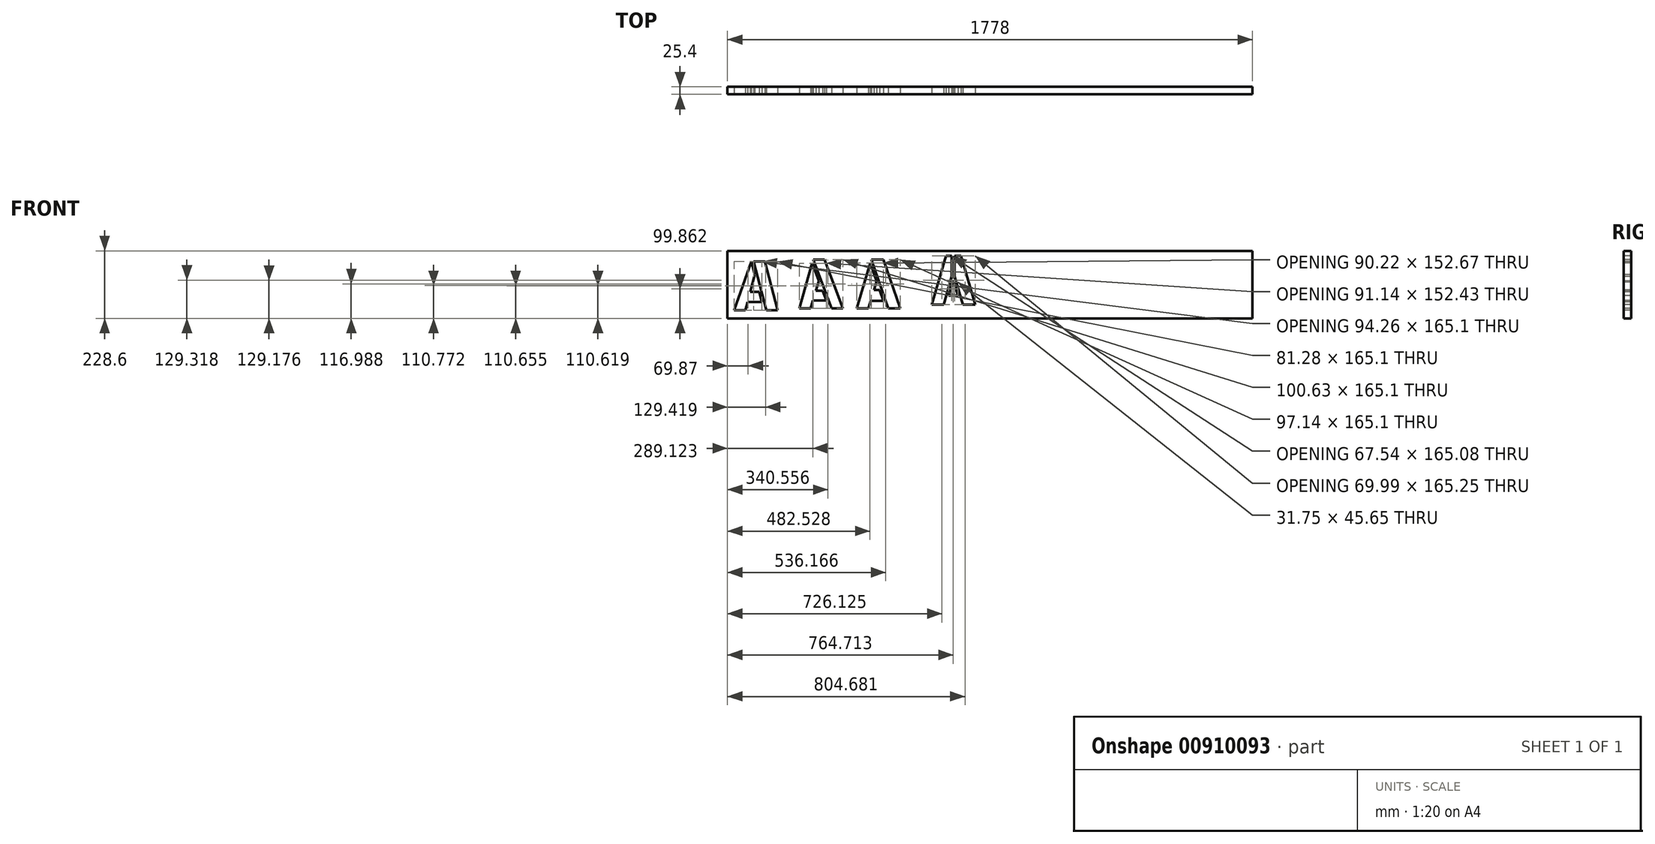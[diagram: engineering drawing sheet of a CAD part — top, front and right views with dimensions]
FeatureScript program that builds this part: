
annotation { "Feature Type Name" : "Feature", "Feature Type Description" : "" }
export const myFeature = defineFeature(function(context is Context, id is Id, definition is map)
    precondition{}
    {
        {
            var Q0;
            Q0=qCreatedBy(makeId("Front.planeOp"),FACE);
            var sketch = newSketch(context, id + "F0", { "sketchPlane" : qUnion([Q0])});
            skLineSegment(sketch, "E0.bottom", {"start": v(-868.11, -370.2) * mm, "end": v(909.89, -370.2) * mm});
            skLineSegment(sketch, "E0.top", {"start": v(-868.11, -598.8) * mm, "end": v(909.89, -598.8) * mm});
            skLineSegment(sketch, "E0.left", {"start": v(-868.11, -370.2) * mm, "end": v(-868.11, -598.8) * mm});
            skLineSegment(sketch, "E0.right", {"start": v(909.89, -370.2) * mm, "end": v(909.89, -598.8) * mm});
            skSolve(sketch);
        }
        {
            var Q0;
            Q0=makeQuery(id+"F0.imprint","IMPRINT",FACE,{"disambiguationData":[TD([[makeQuery(id+"F0.imprint","IMPRINT",EDGE,{"derivedFrom":sQuery(id+"F0.wireOp",EDGE,"E0.bottom")}),-1.0]])]});
            extrude(context, id + "F1", {"entities" : qUnion([Q0]), "depth" : 25.4 * mm, "offsetDistance" : 25.4 * mm});
        }
        {
            var Q0;
            Q0=makeQuery(id+"F1.opExtrude","CAP_FACE",FACE,{"disambiguationData":[OSD([sQuery(id+"F0.wireOp",EDGE,"E0.bottom"),sQuery(id+"F0.wireOp",EDGE,"E0.top"),sQuery(id+"F0.wireOp",EDGE,"E0.left"),sQuery(id+"F0.wireOp",EDGE,"E0.right")])],"isStart":false});
            var sketch = newSketch(context, id + "F2", { "sketchPlane" : qUnion([Q0])});
            skLineSegment(sketch, "E1", {"start": v(-845.37, -570.74) * mm, "end": v(-807.27, -570.74) * mm});
            skLineSegment(sketch, "E2", {"start": v(-807.27, -570.74) * mm, "end": v(-800.17, -543.64) * mm});
            skLineSegment(sketch, "E3", {"start": v(-790.36, -508.6) * mm, "end": v(-775.3, -451.16) * mm});
            skLineSegment(sketch, "E4", {"start": v(-736.15, -570.74) * mm, "end": v(-779.33, -405.64) * mm});
            skLineSegment(sketch, "E5", {"start": v(-779.33, -405.64) * mm, "end": v(-741.23, -405.64) * mm});
            skLineSegment(sketch, "E6", {"start": v(-741.23, -405.64) * mm, "end": v(-698.05, -570.74) * mm});
            skLineSegment(sketch, "E7.trimOffspring", {"start": v(-787.2, -405.64) * mm, "end": v(-845.37, -570.74) * mm});
            skLineSegment(sketch, "E8.trimOffspring", {"start": v(-775.3, -451.16) * mm, "end": v(-787.2, -405.64) * mm});
            skLineSegment(sketch, "E9", {"start": v(-736.15, -570.74) * mm, "end": v(-698.05, -570.74) * mm});
            skLineSegment(sketch, "E10", {"start": v(-800.17, -543.64) * mm, "end": v(-751.1, -543.66) * mm});
            skLineSegment(sketch, "E11", {"start": v(-751.1, -543.66) * mm, "end": v(-760.28, -508.61) * mm});
            skLineSegment(sketch, "E12", {"start": v(-760.28, -508.61) * mm, "end": v(-790.36, -508.6) * mm});
            skSolve(sketch);
        }
        {
            var Q0;
            Q0=makeQuery(id+"F2.imprint","IMPRINT",FACE,{"disambiguationData":[TD([[makeQuery(id+"F2.imprint","IMPRINT",EDGE,{"derivedFrom":sQuery(id+"F2.wireOp",EDGE,"E1")}),1.0]])]});
            var Q1;
            Q1=makeQuery(id+"F2.imprint","IMPRINT",FACE,{"disambiguationData":[TD([[makeQuery(id+"F2.imprint","IMPRINT",EDGE,{"derivedFrom":sQuery(id+"F2.wireOp",EDGE,"E4")}),-1.0]])]});
            extrude(context, id + "F3", {"entities" : qUnion([Q0, Q1]), "operationType" : NewBodyOperationType.REMOVE, "oppositeDirection" : true, "depth" : 25.4 * mm, "offsetDistance" : 25.4 * mm});
        }
        {
            var Q0;
            Q0=makeQuery(id+"F1.opExtrude","CAP_FACE",FACE,{"disambiguationData":[OSD([sQuery(id+"F0.wireOp",EDGE,"E0.bottom"),sQuery(id+"F0.wireOp",EDGE,"E0.top"),sQuery(id+"F0.wireOp",EDGE,"E0.left"),sQuery(id+"F0.wireOp",EDGE,"E0.right")])],"isStart":false});
            var sketch = newSketch(context, id + "F4", { "sketchPlane" : qUnion([Q0])});
            skLineSegment(sketch, "E13", {"start": v(-624.56, -564.37) * mm, "end": v(-586.46, -564.37) * mm});
            skLineSegment(sketch, "E14", {"start": v(-586.46, -564.37) * mm, "end": v(-579, -538.16) * mm});
            skLineSegment(sketch, "E15", {"start": v(-568.16, -505.31) * mm, "end": v(-558.6, -471.68) * mm});
            skLineSegment(sketch, "E16", {"start": v(-515.34, -564.37) * mm, "end": v(-577.87, -399.27) * mm});
            skLineSegment(sketch, "E17", {"start": v(-577.87, -399.27) * mm, "end": v(-539.77, -399.27) * mm});
            skLineSegment(sketch, "E18", {"start": v(-539.77, -399.27) * mm, "end": v(-477.24, -564.37) * mm});
            skLineSegment(sketch, "E19.trimOffspring", {"start": v(-581.22, -411.94) * mm, "end": v(-624.56, -564.37) * mm});
            skLineSegment(sketch, "E20", {"start": v(-515.34, -564.37) * mm, "end": v(-477.24, -564.37) * mm});
            skLineSegment(sketch, "E21", {"start": v(-579, -538.16) * mm, "end": v(-533.41, -538.16) * mm});
            skLineSegment(sketch, "E22", {"start": v(-533.41, -538.16) * mm, "end": v(-545.86, -505.31) * mm});
            skLineSegment(sketch, "E23", {"start": v(-545.86, -505.31) * mm, "end": v(-568.16, -505.31) * mm});
            skLineSegment(sketch, "E24", {"start": v(-581.22, -411.94) * mm, "end": v(-558.6, -471.68) * mm});
            skSolve(sketch);
        }
        {
            var Q0;
            Q0=makeQuery(id+"F4.imprint","IMPRINT",FACE,{"disambiguationData":[TD([[makeQuery(id+"F4.imprint","IMPRINT",EDGE,{"derivedFrom":sQuery(id+"F4.wireOp",EDGE,"E16")}),-1.0]])]});
            var Q1;
            Q1=makeQuery(id+"F4.imprint","IMPRINT",FACE,{"disambiguationData":[TD([[makeQuery(id+"F4.imprint","IMPRINT",EDGE,{"derivedFrom":sQuery(id+"F4.wireOp",EDGE,"E13")}),1.0]])]});
            extrude(context, id + "F5", {"entities" : qUnion([Q0, Q1]), "operationType" : NewBodyOperationType.REMOVE, "oppositeDirection" : true, "depth" : 25.4 * mm, "offsetDistance" : 25.4 * mm});
        }
        {
            var Q0;
            Q0=makeQuery(id+"F1.opExtrude","CAP_FACE",FACE,{"disambiguationData":[OSD([sQuery(id+"F0.wireOp",EDGE,"E0.bottom"),sQuery(id+"F0.wireOp",EDGE,"E0.top"),sQuery(id+"F0.wireOp",EDGE,"E0.left"),sQuery(id+"F0.wireOp",EDGE,"E0.right")])],"isStart":false});
            var sketch = newSketch(context, id + "F6", { "sketchPlane" : qUnion([Q0])});
            skLineSegment(sketch, "E25", {"start": v(-430.7, -564.37) * mm, "end": v(-390.87, -564.37) * mm});
            skLineSegment(sketch, "E26", {"start": v(-390.87, -564.37) * mm, "end": v(-363.14, -473.13) * mm});
            skLineSegment(sketch, "E27", {"start": v(-363.14, -473.13) * mm, "end": v(-384.3, -411.7) * mm});
            skLineSegment(sketch, "E28", {"start": v(-380.52, -399.27) * mm, "end": v(-340.22, -399.27) * mm});
            skLineSegment(sketch, "E29", {"start": v(-340.22, -399.27) * mm, "end": v(-283.37, -564.37) * mm});
            skLineSegment(sketch, "E30", {"start": v(-283.37, -564.37) * mm, "end": v(-323.67, -564.37) * mm});
            skLineSegment(sketch, "E31", {"start": v(-323.67, -564.37) * mm, "end": v(-380.52, -399.27) * mm});
            skLineSegment(sketch, "E32", {"start": v(-383.15, -538.97) * mm, "end": v(-340.47, -538.97) * mm});
            skLineSegment(sketch, "E33", {"start": v(-340.47, -538.97) * mm, "end": v(-352.88, -502.95) * mm});
            skLineSegment(sketch, "E34", {"start": v(-352.88, -502.95) * mm, "end": v(-372.2, -502.95) * mm});
            skLineSegment(sketch, "E35", {"start": v(-430.7, -564.37) * mm, "end": v(-374.4, -379.12) * mm});
            skSolve(sketch);
        }
        {
            var Q0;
            {var subQ3=sQuery(id+"F6.wireOp",EDGE,"E25");Q0=makeQuery(id+"F6.imprint","IMPRINT",FACE,{"disambiguationData":[TD([[makeQuery(id+"F6.imprint","IMPRINT",EDGE,{"derivedFrom":subQ3}),1.0]])]});}
            var Q1;
            {var subQ0=sQuery(id+"F6.wireOp",EDGE,"E32");Q1=makeQuery(id+"F6.imprint","IMPRINT",FACE,{"disambiguationData":[TD([[makeQuery(id+"F6.imprint","IMPRINT",EDGE,{"derivedFrom":subQ0}),1.0]])]});}
            var Q2;
            Q2=makeQuery(id+"F6.imprint","IMPRINT",FACE,{"disambiguationData":[TD([[makeQuery(id+"F6.imprint","IMPRINT",EDGE,{"derivedFrom":sQuery(id+"F6.wireOp",EDGE,"E28")}),-1.0]])]});
            extrude(context, id + "F7", {"entities" : qUnion([Q0, Q1, Q2]), "operationType" : NewBodyOperationType.REMOVE, "oppositeDirection" : true, "depth" : 25.4 * mm, "offsetDistance" : 25.4 * mm});
        }
        {
            var Q0;
            Q0=makeQuery(id+"F1.opExtrude","CAP_FACE",FACE,{"disambiguationData":[OSD([sQuery(id+"F0.wireOp",EDGE,"E0.bottom"),sQuery(id+"F0.wireOp",EDGE,"E0.top"),sQuery(id+"F0.wireOp",EDGE,"E0.left"),sQuery(id+"F0.wireOp",EDGE,"E0.right")])],"isStart":false});
            var sketch = newSketch(context, id + "F8", { "sketchPlane" : qUnion([Q0])});
            skLineSegment(sketch, "E36", {"start": v(-127.49, -386.95) * mm, "end": v(-108.22, -387) * mm});
            skLineSegment(sketch, "E37", {"start": v(-76.69, -387.06) * mm, "end": v(-28.43, -552.26) * mm});
            skLineSegment(sketch, "E38", {"start": v(-28.43, -552.26) * mm, "end": v(-70.7, -552.17) * mm});
            skLineSegment(sketch, "E39", {"start": v(-136.08, -552.03) * mm, "end": v(-175.75, -551.95) * mm});
            skLineSegment(sketch, "E40", {"start": v(-127.49, -386.95) * mm, "end": v(-175.75, -551.95) * mm});
            skLineSegment(sketch, "E41", {"start": v(-136.08, -552.03) * mm, "end": v(-108.36, -457.27) * mm});
            skLineSegment(sketch, "E42", {"start": v(-70.7, -552.17) * mm, "end": v(-98.42, -457.27) * mm});
            skLineSegment(sketch, "E43", {"start": v(-108.22, -387) * mm, "end": v(-108.36, -457.27) * mm});
            skLineSegment(sketch, "E44", {"start": v(-98.42, -457.27) * mm, "end": v(-98.28, -387.01) * mm});
            skLineSegment(sketch, "E45", {"start": v(-119.27, -521.7) * mm, "end": v(-105.94, -476.12) * mm});
            skLineSegment(sketch, "E46", {"start": v(-100.86, -476.12) * mm, "end": v(-87.52, -521.77) * mm});
            skLineSegment(sketch, "E47", {"start": v(-87.52, -521.77) * mm, "end": v(-119.27, -521.7) * mm});
            skLineSegment(sketch, "E48.trimOffspring", {"start": v(-98.28, -387.01) * mm, "end": v(-76.69, -387.06) * mm});
            skLineSegment(sketch, "E49.bottom", {"start": v(-105.94, -476.12) * mm, "end": v(-100.86, -476.12) * mm});
            skPoint(sketch, "E50.orphan", {"position": v(-103.4, -467.43) * mm});
            skSolve(sketch);
        }
        {
            var Q0;
            Q0=makeQuery(id+"F8.imprint","IMPRINT",FACE,{"disambiguationData":[TD([[makeQuery(id+"F8.imprint","IMPRINT",EDGE,{"derivedFrom":sQuery(id+"F8.wireOp",EDGE,"y6zHQ2HE-tir1-FnWy-CZTN-8O3FpK8Fo0QJ")}),-1.0]])]});
            var Q1;
            {var subQ1=sQuery(id+"F8.wireOp",EDGE,"aWlimi2E-Ho2b-eYf1-UKuN-SSchGj3vamK0");Q1=makeQuery(id+"F8.imprint","IMPRINT",FACE,{"disambiguationData":[TD([[makeQuery(id+"F8.imprint","IMPRINT",EDGE,{"derivedFrom":subQ1}),-1.0]])]});}
            var Q2;
            Q2=makeQuery(id+"F8.imprint","IMPRINT",FACE,{"disambiguationData":[TD([[makeQuery(id+"F8.imprint","IMPRINT",EDGE,{"derivedFrom":sQuery(id+"F8.wireOp",EDGE,"S3InjjKa-XbD2-Fcau-L1xh-OMRDJGx4FW1W")}),-1.0]])]});
            var Q3;
            Q3=makeQuery(id+"F8.imprint","IMPRINT",FACE,{"disambiguationData":[TD([[makeQuery(id+"F8.imprint","IMPRINT",EDGE,{"derivedFrom":sQuery(id+"F8.wireOp",EDGE,"QMrmG2ib-1jLl-hlU9-aHOm-9F3mrlCaxFKU")}),-1.0]])]});
            var Q4;
            {var subQ1=sQuery(id+"F8.wireOp",EDGE,"E39");Q4=makeQuery(id+"F8.imprint","IMPRINT",FACE,{"disambiguationData":[TD([[makeQuery(id+"F8.imprint","IMPRINT",EDGE,{"derivedFrom":subQ1}),-1.0]])]});}
            var Q5;
            Q5=makeQuery(id+"F8.imprint","IMPRINT",FACE,{"disambiguationData":[TD([[makeQuery(id+"F8.imprint","IMPRINT",EDGE,{"derivedFrom":sQuery(id+"F8.wireOp",EDGE,"E45")}),-1.0]])]});
            var Q6;
            {var subQ4=sQuery(id+"F8.wireOp",EDGE,"E37");Q6=makeQuery(id+"F8.imprint","IMPRINT",FACE,{"disambiguationData":[TD([[makeQuery(id+"F8.imprint","IMPRINT",EDGE,{"derivedFrom":subQ4}),-1.0]])]});}
            extrude(context, id + "F9", {"entities" : qUnion([Q0, Q1, Q2, Q3, Q4, Q5, Q6]), "operationType" : NewBodyOperationType.REMOVE, "oppositeDirection" : true, "depth" : 25.4 * mm, "offsetDistance" : 25.4 * mm});
        }
    });
